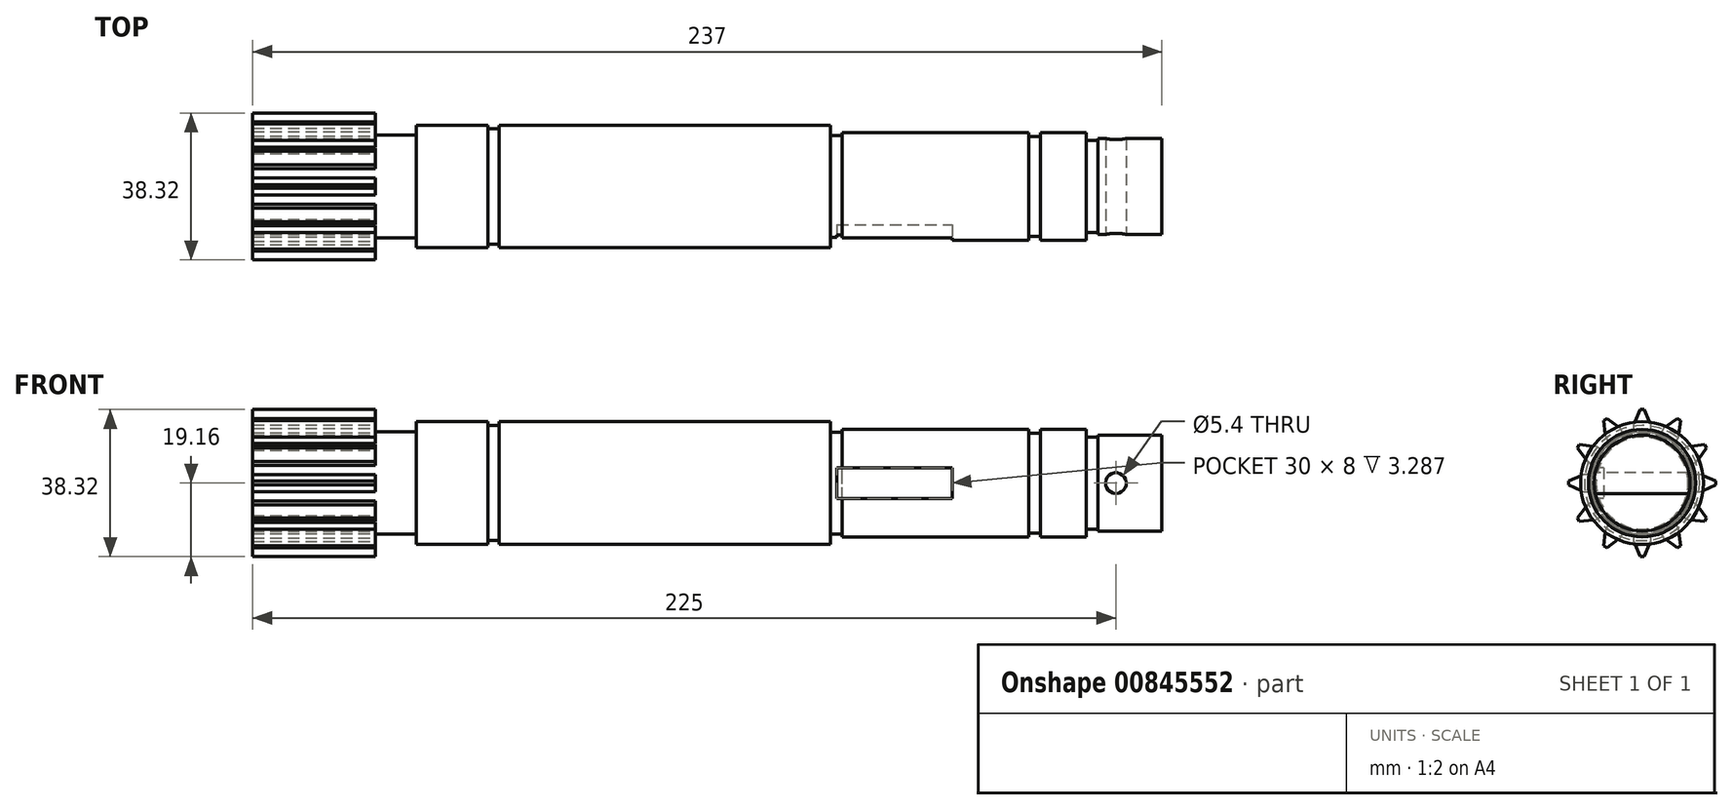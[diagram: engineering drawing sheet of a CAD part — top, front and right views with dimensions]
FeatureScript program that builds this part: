
annotation { "Feature Type Name" : "Feature", "Feature Type Description" : "" }
export const myFeature = defineFeature(function(context is Context, id is Id, definition is map)
    precondition{}
    {
        {
            var Q0;
            Q0=qCreatedBy(makeId("Front.planeOp"),FACE);
            var sketch = newSketch(context, id + "F0", { "sketchPlane" : qUnion([Q0])});
            skLineSegment(sketch, "E0", {"start": v(10.7, 16) * mm, "end": v(29.3, 16) * mm});
            skLineSegment(sketch, "E1", {"start": v(32.3, 16) * mm, "end": v(118.6, 16) * mm});
            skLineSegment(sketch, "E2", {"start": v(118.6, 16) * mm, "end": v(118.6, 13.3) * mm});
            skLineSegment(sketch, "E3", {"start": v(118.6, 13.3) * mm, "end": v(121.6, 13.3) * mm});
            skLineSegment(sketch, "E4", {"start": v(121.6, 13.3) * mm, "end": v(121.6, 14) * mm});
            skLineSegment(sketch, "E5", {"start": v(121.6, 14) * mm, "end": v(170.3, 14) * mm});
            skLineSegment(sketch, "E6", {"start": v(170.3, 14) * mm, "end": v(170.3, 13) * mm});
            skLineSegment(sketch, "E7", {"start": v(170.3, 13) * mm, "end": v(173.3, 13) * mm});
            skLineSegment(sketch, "E8", {"start": v(173.3, 14) * mm, "end": v(185.3, 14) * mm});
            skLineSegment(sketch, "E9", {"start": v(185.3, 14) * mm, "end": v(185.3, 12) * mm});
            skLineSegment(sketch, "E10", {"start": v(185.3, 12) * mm, "end": v(188.3, 12) * mm});
            skLineSegment(sketch, "E11", {"start": v(188.3, 12) * mm, "end": v(188.3, 12.5) * mm});
            skLineSegment(sketch, "E12", {"start": v(188.3, 12.5) * mm, "end": v(205, 12.5) * mm});
            skLineSegment(sketch, "E13", {"start": v(205, 12.5) * mm, "end": v(205, 0) * mm});
            skLineSegment(sketch, "E14", {"start": v(205, 0) * mm, "end": v(0, 0) * mm});
            skLineSegment(sketch, "E15", {"start": v(173.3, 13) * mm, "end": v(173.3, 14) * mm});
            skLineSegment(sketch, "E16", {"start": v(29.3, 16) * mm, "end": v(29.3, 15) * mm});
            skLineSegment(sketch, "E17", {"start": v(29.3, 15) * mm, "end": v(32.3, 15) * mm});
            skLineSegment(sketch, "E18", {"start": v(32.3, 15) * mm, "end": v(32.3, 16) * mm});
            skLineSegment(sketch, "E19", {"start": v(10.7, 16) * mm, "end": v(10.7, 13.35) * mm});
            skLineSegment(sketch, "E20", {"start": v(10.7, 13.35) * mm, "end": v(0, 13.35) * mm});
            skLineSegment(sketch, "E21", {"start": v(0, 13.35) * mm, "end": v(0, 0) * mm});
            skSolve(sketch);
        }
        {
            var Q0;
            Q0=makeQuery(id+"F0.imprint","IMPRINT",FACE,{"disambiguationData":[TD([[makeQuery(id+"F0.imprint","IMPRINT",EDGE,{"derivedFrom":sQuery(id+"F0.wireOp",EDGE,"E0")}),-1.0]])]});
            var Q1;
            Q1=sQuery(id+"F0.wireOp",EDGE,"E14");
            revolve(context, id + "F1", {"surfaceOperationType" : NewSurfaceOperationType.NEW, "entities" : qUnion([Q0]), "axis" : qUnion([Q1]), "revolveType" : RevolveType.FULL});
        }
        {
            var Q0;
            Q0=makeQuery(id+"F1.opRevolve","SWEPT_FACE",FACE,{"disambiguationData":[OSD([sQuery(id+"F0.wireOp",EDGE,"E21")])]});
            var sketch = newSketch(context, id + "F2", { "sketchPlane" : qUnion([Q0])});
            skLineSegment(sketch, "E22", {"start": v(-2.25, 13.16) * mm, "end": v(-2.25, 15.16) * mm});
            skLineSegment(sketch, "E23", {"start": v(-2.25, 15.16) * mm, "end": v(-0.5, 19.16) * mm});
            skLineSegment(sketch, "E24", {"start": v(-0.5, 19.16) * mm, "end": v(0.5, 19.16) * mm});
            skLineSegment(sketch, "E25", {"start": v(0.5, 19.16) * mm, "end": v(2.25, 15.16) * mm});
            skLineSegment(sketch, "E26", {"start": v(2.25, 15.16) * mm, "end": v(2.25, 13.16) * mm});
            skLineSegment(sketch, "E27.1.0", {"start": v(-9.15, 16.84) * mm, "end": v(-5.63, 14.25) * mm});
            skLineSegment(sketch, "E27.1.1", {"start": v(-9.53, 12) * mm, "end": v(-10.01, 16.34) * mm});
            skLineSegment(sketch, "E27.1.2", {"start": v(-5.63, 14.25) * mm, "end": v(-4.63, 12.52) * mm});
            skLineSegment(sketch, "E27.1.3", {"start": v(-8.53, 10.27) * mm, "end": v(-9.53, 12) * mm});
            skLineSegment(sketch, "E27.1.5", {"start": v(-10.01, 16.34) * mm, "end": v(-9.15, 16.84) * mm});
            skLineSegment(sketch, "E27.2.0", {"start": v(-16.34, 10.01) * mm, "end": v(-12, 9.53) * mm});
            skLineSegment(sketch, "E27.2.1", {"start": v(-14.25, 5.63) * mm, "end": v(-16.84, 9.15) * mm});
            skLineSegment(sketch, "E27.2.2", {"start": v(-12, 9.53) * mm, "end": v(-10.27, 8.53) * mm});
            skLineSegment(sketch, "E27.2.3", {"start": v(-12.52, 4.63) * mm, "end": v(-14.25, 5.63) * mm});
            skLineSegment(sketch, "E27.2.5", {"start": v(-16.84, 9.15) * mm, "end": v(-16.34, 10.01) * mm});
            skLineSegment(sketch, "E27.3.0", {"start": v(-19.16, 0.5) * mm, "end": v(-15.16, 2.25) * mm});
            skLineSegment(sketch, "E27.3.1", {"start": v(-15.16, -2.25) * mm, "end": v(-19.16, -0.5) * mm});
            skLineSegment(sketch, "E27.3.2", {"start": v(-15.16, 2.25) * mm, "end": v(-13.16, 2.25) * mm});
            skLineSegment(sketch, "E27.3.3", {"start": v(-13.16, -2.25) * mm, "end": v(-15.16, -2.25) * mm});
            skLineSegment(sketch, "E27.3.5", {"start": v(-19.16, -0.5) * mm, "end": v(-19.16, 0.5) * mm});
            skLineSegment(sketch, "E27.4.0", {"start": v(-16.84, -9.15) * mm, "end": v(-14.25, -5.63) * mm});
            skLineSegment(sketch, "E27.4.1", {"start": v(-12, -9.53) * mm, "end": v(-16.34, -10.01) * mm});
            skLineSegment(sketch, "E27.4.2", {"start": v(-14.25, -5.63) * mm, "end": v(-12.52, -4.63) * mm});
            skLineSegment(sketch, "E27.4.3", {"start": v(-10.27, -8.53) * mm, "end": v(-12, -9.53) * mm});
            skLineSegment(sketch, "E27.4.5", {"start": v(-16.34, -10.01) * mm, "end": v(-16.84, -9.15) * mm});
            skLineSegment(sketch, "E27.5.0", {"start": v(-10.01, -16.34) * mm, "end": v(-9.53, -12) * mm});
            skLineSegment(sketch, "E27.5.1", {"start": v(-5.63, -14.25) * mm, "end": v(-9.15, -16.84) * mm});
            skLineSegment(sketch, "E27.5.2", {"start": v(-9.53, -12) * mm, "end": v(-8.53, -10.27) * mm});
            skLineSegment(sketch, "E27.5.3", {"start": v(-4.63, -12.52) * mm, "end": v(-5.63, -14.25) * mm});
            skLineSegment(sketch, "E27.5.5", {"start": v(-9.15, -16.84) * mm, "end": v(-10.01, -16.34) * mm});
            skLineSegment(sketch, "E27.6.0", {"start": v(-0.5, -19.16) * mm, "end": v(-2.25, -15.16) * mm});
            skLineSegment(sketch, "E27.6.1", {"start": v(2.25, -15.16) * mm, "end": v(0.5, -19.16) * mm});
            skLineSegment(sketch, "E27.6.2", {"start": v(-2.25, -15.16) * mm, "end": v(-2.25, -13.16) * mm});
            skLineSegment(sketch, "E27.6.3", {"start": v(2.25, -13.16) * mm, "end": v(2.25, -15.16) * mm});
            skLineSegment(sketch, "E27.6.5", {"start": v(0.5, -19.16) * mm, "end": v(-0.5, -19.16) * mm});
            skLineSegment(sketch, "E27.7.0", {"start": v(9.15, -16.84) * mm, "end": v(5.63, -14.25) * mm});
            skLineSegment(sketch, "E27.7.1", {"start": v(9.53, -12) * mm, "end": v(10.01, -16.34) * mm});
            skLineSegment(sketch, "E27.7.2", {"start": v(5.63, -14.25) * mm, "end": v(4.63, -12.52) * mm});
            skLineSegment(sketch, "E27.7.3", {"start": v(8.53, -10.27) * mm, "end": v(9.53, -12) * mm});
            skLineSegment(sketch, "E27.7.5", {"start": v(10.01, -16.34) * mm, "end": v(9.15, -16.84) * mm});
            skLineSegment(sketch, "E27.8.0", {"start": v(16.34, -10.01) * mm, "end": v(12, -9.53) * mm});
            skLineSegment(sketch, "E27.8.1", {"start": v(14.25, -5.63) * mm, "end": v(16.84, -9.15) * mm});
            skLineSegment(sketch, "E27.8.2", {"start": v(12, -9.53) * mm, "end": v(10.27, -8.53) * mm});
            skLineSegment(sketch, "E27.8.3", {"start": v(12.52, -4.63) * mm, "end": v(14.25, -5.63) * mm});
            skLineSegment(sketch, "E27.8.5", {"start": v(16.84, -9.15) * mm, "end": v(16.34, -10.01) * mm});
            skLineSegment(sketch, "E27.9.0", {"start": v(19.16, -0.5) * mm, "end": v(15.16, -2.25) * mm});
            skLineSegment(sketch, "E27.9.1", {"start": v(15.16, 2.25) * mm, "end": v(19.16, 0.5) * mm});
            skLineSegment(sketch, "E27.9.2", {"start": v(15.16, -2.25) * mm, "end": v(13.16, -2.25) * mm});
            skLineSegment(sketch, "E27.9.3", {"start": v(13.16, 2.25) * mm, "end": v(15.16, 2.25) * mm});
            skLineSegment(sketch, "E27.9.5", {"start": v(19.16, 0.5) * mm, "end": v(19.16, -0.5) * mm});
            skLineSegment(sketch, "E27.10.0", {"start": v(16.84, 9.15) * mm, "end": v(14.25, 5.63) * mm});
            skLineSegment(sketch, "E27.10.1", {"start": v(12, 9.53) * mm, "end": v(16.34, 10.01) * mm});
            skLineSegment(sketch, "E27.10.2", {"start": v(14.25, 5.63) * mm, "end": v(12.52, 4.63) * mm});
            skLineSegment(sketch, "E27.10.3", {"start": v(10.27, 8.53) * mm, "end": v(12, 9.53) * mm});
            skLineSegment(sketch, "E27.10.5", {"start": v(16.34, 10.01) * mm, "end": v(16.84, 9.15) * mm});
            skLineSegment(sketch, "E27.11.0", {"start": v(10.01, 16.34) * mm, "end": v(9.53, 12) * mm});
            skLineSegment(sketch, "E27.11.1", {"start": v(5.63, 14.25) * mm, "end": v(9.15, 16.84) * mm});
            skLineSegment(sketch, "E27.11.2", {"start": v(9.53, 12) * mm, "end": v(8.53, 10.27) * mm});
            skLineSegment(sketch, "E27.11.3", {"start": v(4.63, 12.52) * mm, "end": v(5.63, 14.25) * mm});
            skLineSegment(sketch, "E27.11.5", {"start": v(9.15, 16.84) * mm, "end": v(10.01, 16.34) * mm});
            skPoint(sketch, "E27.center", {"position": v(0, 0) * mm});
            skSolve(sketch);
        }
        {
            var Q0;
            Q0=makeQuery(id+"F2.imprint","IMPRINT",FACE,{"disambiguationData":[TD([[makeQuery(id+"F2.imprint","IMPRINT",EDGE,{"derivedFrom":sQuery(id+"F2.wireOp",EDGE,"E27.1.0")}),-1.0]])]});
            var Q1;
            Q1=makeQuery(id+"F2.imprint","IMPRINT",FACE,{"disambiguationData":[TD([[makeQuery(id+"F2.imprint","IMPRINT",EDGE,{"derivedFrom":sQuery(id+"F2.wireOp",EDGE,"E22")}),-1.0]])]});
            var Q2;
            {var subQ2=sQuery(id+"F2.wireOp",EDGE,"E27.11.0");Q2=makeQuery(id+"F2.imprint","IMPRINT",FACE,{"disambiguationData":[TD([[makeQuery(id+"F2.imprint","IMPRINT",EDGE,{"derivedFrom":subQ2}),-1.0]])]});}
            var Q3;
            {var subQ5=sQuery(id+"F2.wireOp",EDGE,"E27.10.0");Q3=makeQuery(id+"F2.imprint","IMPRINT",FACE,{"disambiguationData":[TD([[makeQuery(id+"F2.imprint","IMPRINT",EDGE,{"derivedFrom":subQ5}),-1.0]])]});}
            var Q4;
            {var subQ5=sQuery(id+"F2.wireOp",EDGE,"E27.9.0");Q4=makeQuery(id+"F2.imprint","IMPRINT",FACE,{"disambiguationData":[TD([[makeQuery(id+"F2.imprint","IMPRINT",EDGE,{"derivedFrom":subQ5}),-1.0]])]});}
            var Q5;
            {var subQ5=sQuery(id+"F2.wireOp",EDGE,"E27.8.0");Q5=makeQuery(id+"F2.imprint","IMPRINT",FACE,{"disambiguationData":[TD([[makeQuery(id+"F2.imprint","IMPRINT",EDGE,{"derivedFrom":subQ5}),-1.0]])]});}
            var Q6;
            Q6=makeQuery(id+"F2.imprint","IMPRINT",FACE,{"disambiguationData":[TD([[makeQuery(id+"F2.imprint","IMPRINT",EDGE,{"derivedFrom":sQuery(id+"F2.wireOp",EDGE,"E27.7.0")}),-1.0]])]});
            var Q7;
            Q7=makeQuery(id+"F2.imprint","IMPRINT",FACE,{"disambiguationData":[TD([[makeQuery(id+"F2.imprint","IMPRINT",EDGE,{"derivedFrom":sQuery(id+"F2.wireOp",EDGE,"E27.6.0")}),-1.0]])]});
            var Q8;
            Q8=makeQuery(id+"F2.imprint","IMPRINT",FACE,{"disambiguationData":[TD([[makeQuery(id+"F2.imprint","IMPRINT",EDGE,{"derivedFrom":sQuery(id+"F2.wireOp",EDGE,"E27.5.0")}),-1.0]])]});
            var Q9;
            Q9=makeQuery(id+"F2.imprint","IMPRINT",FACE,{"disambiguationData":[TD([[makeQuery(id+"F2.imprint","IMPRINT",EDGE,{"derivedFrom":sQuery(id+"F2.wireOp",EDGE,"E27.4.0")}),-1.0]])]});
            var Q10;
            Q10=makeQuery(id+"F2.imprint","IMPRINT",FACE,{"disambiguationData":[TD([[makeQuery(id+"F2.imprint","IMPRINT",EDGE,{"derivedFrom":sQuery(id+"F2.wireOp",EDGE,"E27.3.0")}),-1.0]])]});
            var Q11;
            Q11=makeQuery(id+"F2.imprint","IMPRINT",FACE,{"disambiguationData":[TD([[makeQuery(id+"F2.imprint","IMPRINT",EDGE,{"derivedFrom":sQuery(id+"F2.wireOp",EDGE,"E27.2.0")}),-1.0]])]});
            var Q12;
            {var subQ1=makeQuery(id+"F1.opRevolve","SWEPT_EDGE",EDGE,{"disambiguationData":[OSD([sQuery(id+"F0.wireOp",EDGE,"E20"),sQuery(id+"F0.wireOp",EDGE,"E21")])]});var subQ4=sQuery(id+"F2.wireOp",EDGE,"E27.7.4");var subQ5=makeQuery(id+"F2.imprint","INTERSECT",VERTEX,{"derivedFrom":[subQ1,sQuery(id+"F2.wireOp",EDGE,"E27.7.3"),subQ4]});Q12=makeQuery(id+"F2.imprint","IMPRINT",FACE,{"disambiguationData":[TD([[makeQuery(id+"F2.imprint","IMPRINT",EDGE,{"disambiguationData":[TD([[subQ5,1.0]])],"derivedFrom":subQ1}),-1.0]])]});}
            extrude(context, id + "F3", {"entities" : qUnion([Q0, Q1, Q2, Q3, Q4, Q5, Q6, Q7, Q8, Q9, Q10, Q11, Q12]), "operationType" : NewBodyOperationType.ADD, "depth" : 32 * mm, "offsetDistance" : 25 * mm});
        }
        {
            var Q0;
            Q0=qCreatedBy(makeId("Front.planeOp"),FACE);
            cPlane(context, id + "F4", {"entities" : qUnion([Q0]), "cplaneType" : CPlaneType.OFFSET, "offset" : 12.5 * mm, "width" : 150 * mm, "height" : 150 * mm});
        }
        {
            var Q0;
            Q0=qCreatedBy(id+"F4.planeOp",FACE);
            var sketch = newSketch(context, id + "F5", { "sketchPlane" : qUnion([Q0])});
            skCircle(sketch, "E28", {"center": v(193, 0) * mm, "radius": 2.7 * mm});
            skSolve(sketch);
        }
        {
            var Q0;
            Q0=qCreatedBy(makeId("Front.planeOp"),FACE);
            cPlane(context, id + "F6", {"entities" : qUnion([Q0]), "cplaneType" : CPlaneType.OFFSET, "offset" : 14 * mm, "width" : 150 * mm, "height" : 150 * mm});
        }
        {
            var Q0;
            Q0=qCreatedBy(id+"F6.planeOp",FACE);
            var sketch = newSketch(context, id + "F7", { "sketchPlane" : qUnion([Q0])});
            skLineSegment(sketch, "E29.bottom", {"start": v(120.3, 4) * mm, "end": v(150.3, 4) * mm});
            skLineSegment(sketch, "E29.top", {"start": v(120.3, -4) * mm, "end": v(150.3, -4) * mm});
            skLineSegment(sketch, "E29.left", {"start": v(120.3, 4) * mm, "end": v(120.3, -4) * mm});
            skLineSegment(sketch, "E29.right", {"start": v(150.3, 4) * mm, "end": v(150.3, -4) * mm});
            skSolve(sketch);
        }
        {
            var Q0;
            Q0=makeQuery(id+"F7.imprint","IMPRINT",FACE,{"disambiguationData":[TD([[makeQuery(id+"F7.imprint","IMPRINT",EDGE,{"derivedFrom":sQuery(id+"F7.wireOp",EDGE,"E29.bottom")}),-1.0]])]});
            extrude(context, id + "F8", {"entities" : qUnion([Q0]), "operationType" : NewBodyOperationType.REMOVE, "oppositeDirection" : true, "depth" : 4 * mm, "offsetDistance" : 25 * mm});
        }
        {
            var Q0;
            Q0=makeQuery(id+"F5.imprint","IMPRINT",FACE,{"disambiguationData":[TD([[makeQuery(id+"F5.imprint","IMPRINT",EDGE,{"derivedFrom":sQuery(id+"F5.wireOp",EDGE,"E28")}),1.0]])]});
            extrude(context, id + "F9", {"entities" : qUnion([Q0]), "operationType" : NewBodyOperationType.REMOVE, "oppositeDirection" : true, "depth" : 25 * mm, "offsetDistance" : 25 * mm});
        }
    });
